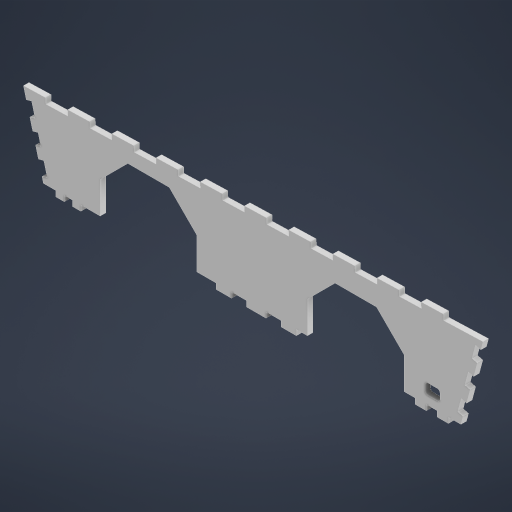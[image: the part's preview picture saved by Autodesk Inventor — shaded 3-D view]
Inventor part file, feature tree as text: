
AUTODESK INVENTOR PART (.ipt)
format: ipt  version: 2023.2 (Build 272271000, 271)  size: 416,256 bytes
history: native  units: mm
features: sketch x2
ambient origin geometry x8: Origin, YZ Plane, XZ Plane, XY Plane, X Axis, Y Axis, Z Axis, Center Point
bodies: Body1 (feature_tree)
feature tree (2):
  sketch  "Sketch1"  dims[d271=105.0deg]
  sketch  "Sketch2"  dims[d273=105.0deg d276=8.0mm d277=6.0mm d278=6.0mm d279=6.0mm d281=11.0mm d282=11.0mm d283=27.0mm d284=14.0mm d285=70.0mm d286=14.0mm d287=14.0mm d288=11.0mm d289=11.0mm d290=8.0mm d297=20.0mm d298=20.0mm d303=70.0mm d304=8.0mm d305=8.0mm d307=8.0mm d308=8.0mm d309=4.0mm d310=4.0mm d311=0.0mm d312=8.0mm d313=10.0mm d314=10.0mm d315=10.0mm d316=10.0mm d319=10.0mm d321=10.0mm d322=10.0mm d323=8.0mm d324=10.0mm d325=8.0mm d326=10.0mm d327=8.0mm d328=8.0mm d329=8.0mm d333=16.0mm d334=16.0mm d339=11.0mm d340=8.0mm d341=2.0mm d342=6.0mm d344=4.0mm d345=0.0mm d346=6.0mm d9=0.5mm d10=0.872665mm d11=0.5mm d12=0.872665mm d13=0.5mm d14=0.872665mm d27=0.5mm d28=0.872665mm d29=0.5mm d30=0.872665mm d88=0.5mm d89=0.872665mm d90=0.5mm d91=0.872665mm d116=0.5mm d117=0.872665mm d118=0.5mm d119=0.872665mm d154=0.5mm d155=0.872665mm d156=0.5mm d157=0.872665mm d181=0.5mm d182=0.872665mm d183=0.5mm d184=0.872665mm d221=0.5mm d222=0.872665mm d223=0.5mm d224=0.872665mm]
